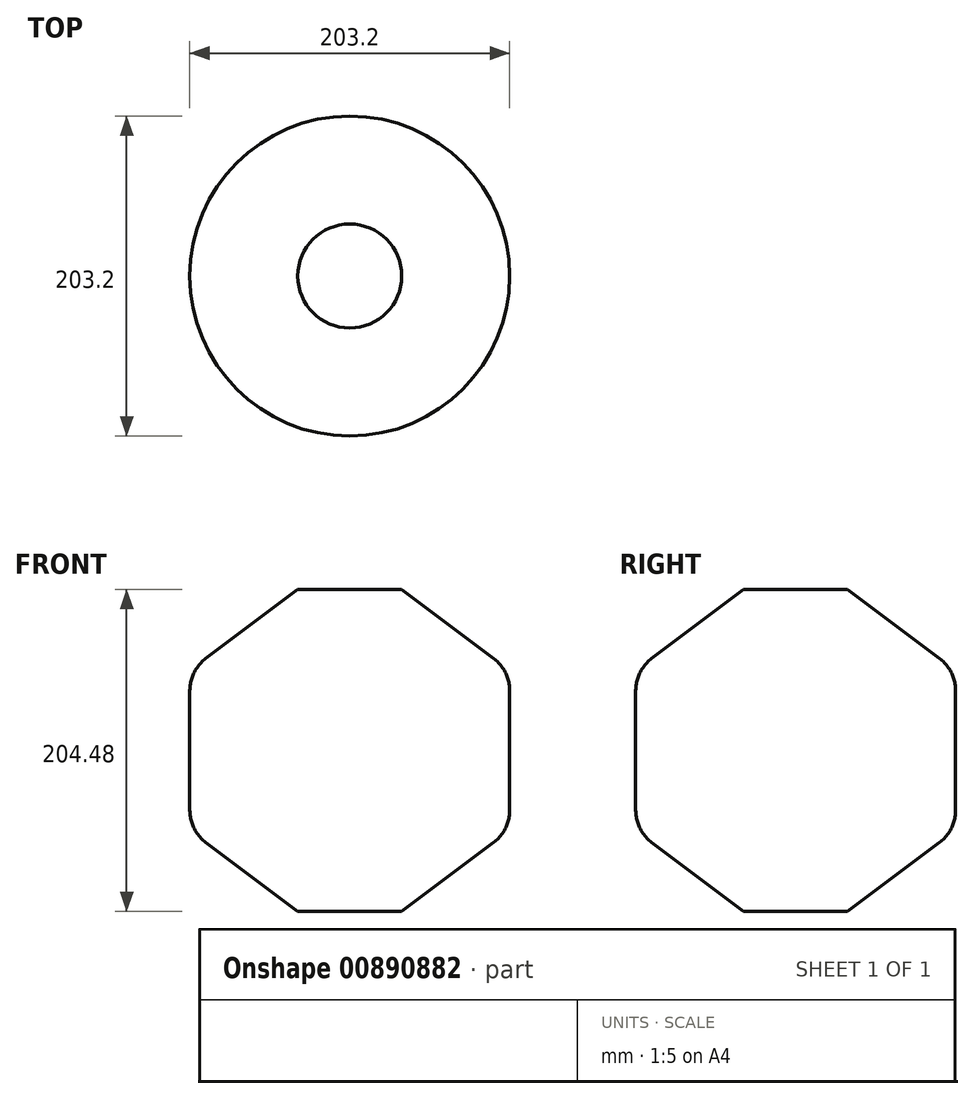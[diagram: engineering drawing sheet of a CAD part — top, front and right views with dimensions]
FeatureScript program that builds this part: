
annotation { "Feature Type Name" : "Feature", "Feature Type Description" : "" }
export const myFeature = defineFeature(function(context is Context, id is Id, definition is map)
    precondition{}
    {
        {
            var Q0;
            Q0=qCreatedBy(makeId("Front.planeOp"),FACE);
            var sketch = newSketch(context, id + "F0", { "sketchPlane" : qUnion([Q0])});
            skLineSegment(sketch, "E0.left", {"start": v(-101.6, 38.1) * mm, "end": v(-101.6, -38.1) * mm});
            skLineSegment(sketch, "E0.right", {"start": v(101.6, 50.8) * mm, "end": v(101.6, -50.8) * mm});
            skLineSegment(sketch, "E1", {"start": v(-91.44, 58.42) * mm, "end": v(-33.02, 102.23) * mm});
            skLineSegment(sketch, "E2", {"start": v(33.02, 102.23) * mm, "end": v(101.6, 50.8) * mm});
            skLineSegment(sketch, "E3", {"start": v(101.6, -50.8) * mm, "end": v(33.02, -102.23) * mm});
            skLineSegment(sketch, "E4", {"start": v(-33.02, -102.24) * mm, "end": v(-91.44, -58.42) * mm});
            skPoint(sketch, "E5.visualSharp", {"position": v(0, 127) * mm});
            skPoint(sketch, "E6.visualSharp", {"position": v(-101.6, 50.8) * mm});
            skArc(sketch, "E6.filletArc", {"start": v(-91.44, 58.42) * mm, "mid": v(-98.92, 49.46) * mm, "end": v(-101.6, 38.1) * mm});
            skPoint(sketch, "E7.visualSharp", {"position": v(-101.6, -50.8) * mm});
            skArc(sketch, "E7.filletArc", {"start": v(-101.6, -38.1) * mm, "mid": v(-98.92, -49.46) * mm, "end": v(-91.44, -58.42) * mm});
            skPoint(sketch, "E8.visualSharp", {"position": v(0, -127) * mm});
            skLineSegment(sketch, "E9", {"start": v(0, 194.24) * mm, "end": v(0, -185.11) * mm});
            skLineSegment(sketch, "E10", {"start": v(-33.02, -102.23) * mm, "end": v(33.02, -102.23) * mm});
            skLineSegment(sketch, "E11", {"start": v(-33.02, 102.23) * mm, "end": v(33.02, 102.23) * mm});
            skSolve(sketch);
        }
        {
            var Q0;
            {var subQ0=sQuery(id+"F0.wireOp",EDGE,"E1");Q0=makeQuery(id+"F0.imprint","IMPRINT",FACE,{"disambiguationData":[TD([[makeQuery(id+"F0.imprint","IMPRINT",EDGE,{"derivedFrom":subQ0}),-1.0]])]});}
            var Q1;
            {var subQ0=sQuery(id+"F0.wireOp",EDGE,"E0.left");Q1=makeQuery(id+"F0.imprint","IMPRINT",FACE,{"disambiguationData":[TD([[makeQuery(id+"F0.imprint","IMPRINT",EDGE,{"derivedFrom":subQ0}),1.0]])]});}
            var Q2;
            {var subQ0=sQuery(id+"F0.wireOp",EDGE,"E4");Q2=makeQuery(id+"F0.imprint","IMPRINT",FACE,{"disambiguationData":[TD([[makeQuery(id+"F0.imprint","IMPRINT",EDGE,{"derivedFrom":subQ0}),-1.0]])]});}
            var Q3;
            Q3=sQuery(id+"F0.wireOp",EDGE,"E9");
            revolve(context, id + "F1", {"surfaceOperationType" : NewSurfaceOperationType.NEW, "entities" : qUnion([Q0, Q1, Q2]), "axis" : qUnion([Q3]), "revolveType" : RevolveType.FULL});
        }
    });
